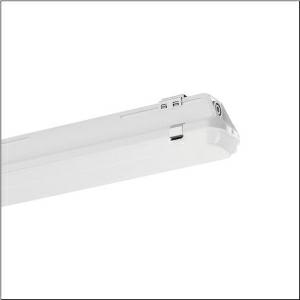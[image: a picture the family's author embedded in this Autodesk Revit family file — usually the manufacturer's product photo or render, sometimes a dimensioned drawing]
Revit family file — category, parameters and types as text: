
# Revit family: monsun_11_51fp20fp460l
name_source: partatom
category: Lighting Fixtures
units: mm (PartAtom-declared; Revit-internal decimal feet)

## family parameters
Cut with Voids When Loaded = No
Host = Face
Light Source = No
Part Type = Normal
Room Calculation Point = No
Round Connector Dimension = Use Diameter
Shared = No

## types (1)
- --- (1 x LED, 5450 lm, 31.5 W, 4000K)
    Apparent Load = 32 VA
    CIE Flux Codes = 45 75 93 94 100
    Color Rendering = 80
    Color Temperature = 4000K
    Default Elevation = 1800 mm
    Description = Monsun 11, damp-proof luminaire, chain hanger, primary optical cover: enclosure, of PC, light emission: direct distribution, primary light characteristic: symmetric, installation type: suspended mounting, surface-mounted, horizontal mounting, vertical mounting, LED, rated luminous flux: 5.450lm, luminous efficacy: 173lm/W, light colour: 840, colour temperature: 4000K, control gear: DALI 2, CLO, with terminal, 5-pole, max. 2.5mm², mains connection: 220..240V, AC, 50/60Hz, rated input power: 32W, luminaire housing, of glass-fibre reinforced polyester, uncoated, bright grey, incl. chain hanger, length: 1.590mm, width: 90mm, height: 88mm, clip for enclosure, of stainless steel (V2A), ceiling mounting element, of stainless steel (V2A), chain hanger, of stainless steel (V2A), protection rating (complete): IP66, insulation class (complete): insulation class I (protective earthing), certification: CE, ENEC, VDE, UKCA, protection symbol: D, impact resistance: IK08, permissible operating ambient temperature: -25..+35°C, standard: EN 50419, EN 60598-2-1, corresponds to IFS (International Featured Standards) requirements for safety and quality in the food industry, for indoor or canopied outdoor use, no direct snow, no direct sun, no direct rain, LABS conformity tested according to VDMA 24364:2018-05, contact your sales advisor before using the luminaires in applications with unclear chemical exposure, large temperature fluctuations or condensation-forming humidity, packaging unit: 1 piece
    Height = 89 mm
    Lamp = 1 x LED
    Lamp Light Flux = 5450 lm
    Lamp Power = 31.5 W
    Lamp count = 1
    Length = 1590 mm
    Luminous efficacy = 173 lm/W
    Manufacturer = Siteco
    ModVariant = No
    Model = 51FP20FP460L
    Mounting Place = Ceiling
    Mounting Type = Surface mounted
    Number of Poles = 1
    OnlyDefault = Yes
    Power Factor = 1
    Product Name = Monsun 11
    Product group = damp-proof luminaire
    ProductGroupID = 300
    Protection Class = Protection class I
    Protection Degree = IP 66
    RLX_Detail_Level = 1
    RLX_Emergency_Light_Flux = 0 lm
    RLX_Emergency_Type = 0
    RLX_Emergency_Type_DB = No
    RlxData = <blob elided: 92613 chars, md5=d95a8db0>
    Socket = socket
    Standby Power = 0 W
    System Light Flux = 5450 lm
    System Power = 32 W
    Type Comments = factory setting: luminous flux: 100 % | dim-lin: 254 | 219 mA
    Type Image = l_1349237.jpg
    URL = http://relux.com
    VarID = @adj_033471
    Voltage = 0 V
    Weight = 0.00 kg
    Width = 90 mm

## geometry (parser evidence)
native form markers: Blend x4, Sweep x12
no freeform markers — native parametric forms only
